# Revit family: CRUi-Red_Amber
name_source: partatom
category: Lighting Fixtures
units: mm (PartAtom-declared; Revit-internal decimal feet)

## family parameters
Always vertical = Yes
Cut with Voids When Loaded = No
Host = Ceiling
Light Source = Yes
OmniClass Number = 23.80.70.11.14.17
OmniClass Title = Direct/Indirect
Part Type = Normal
Room Calculation Point = No
Round Connector Dimension = Use Diameter
Shared = No

## types (14) — shared parameters
Description = LED Cleanroom Recessed Universal
Dimming Lamp Color Temperature Shift = <None>
Emit Shape Visible in Rendering = No
Housing Finish = Metal - Viscor - White
Lamp = LED
Lens Finish = Acrylic - Viscor - Frosted Prismatic P12
Manufacturer = Visioneering By Viscor
Model = CRU
Tilt Angle = 90.00°
URL = https://www.viscor.com
Voltage = 120 V

## per-type parameters (varying)
| type | Apparent Load | Assembly Code | Color Filter | Emit from Rectangle Length | Emit from Rectangle Width | Lamp Wattage | Length | Photometric Web File | Width |
| CRUi-1X4-LED840K35L/35AUNV-DSA | 47 VA |  | 4227327 | 3' - 11 3/4" | 0' - 11 3/4" | 47 VA | 3' - 11 3/4" | CRUi-1X4-LED840K35L_35AUNV-DSA.ies | 0' - 11 3/4" |
| CRUI-2X2-LED840KxxxL/10RUNV-DSA | 30 VA |  | 255 | 1' - 11 3/4" | 1' - 11 3/4" | 30 VA | 1' - 11 3/4" | CRUI-2X2-LED840KxxxL_10RUNV-DSA.ies | 1' - 11 3/4" |
| CRUI-2X4-LED840KxxxL/10RUNV-DSA | 27 VA |  | 255 | 3' - 11 3/4" | 1' - 11 3/4" | 27 VA | 3' - 11 3/4" | CRUI-2X4-LED840KxxxL_10RUNV-DSA.ies | 1' - 11 3/4" |
| CRUi-1X4-LED840K35L/55AUNV-DSA | 74 VA |  | 4227327 | 3' - 11 3/4" | 0' - 11 3/4" | 74 VA | 3' - 11 3/4" | CRUi-1X4-LED840K35L_55AUNV-DSA.ies | 0' - 11 3/4" |
| CRUi-1X4-LED840K35L/70AUNV-DSA | 94 VA |  | 4227327 | 3' - 11 3/4" | 0' - 11 3/4" | 94 VA | 3' - 11 3/4" | CRUi-1X4-LED840K35L_70AUNV-DSA.ies | 0' - 11 3/4" |
| CRUi-1X4-LED840KxxxL/10RUNV-DSA | 31 VA | D5020200 | 255 | 3' - 11 3/4" | 0' - 11 3/4" | 31 VA | 3' - 11 3/4" | CRUi-1X4-LED840KxxxL_10RUNV-DSA.ies | 0' - 11 3/4" |
| CRUi-2X2-LED840KxxxL/35AUNV-DSA | 46 VA |  | 4227327 | 1' - 11 3/4" | 1' - 11 3/4" | 46 VA | 1' - 11 3/4" | CRUi-2X2-LED840KxxxL_35AUNV-DSA.ies | 1' - 11 3/4" |
| CRUi-2X2-LED840KxxxL/55AUNV-DSA | 76 VA |  | 4227327 | 1' - 11 3/4" | 1' - 11 3/4" | 76 VA | 1' - 11 3/4" | CRUi-2X2-LED840KxxxL_55AUNV-DSA.ies | 1' - 11 3/4" |
| CRUi-2X2-LED840KxxxL/70AUNV-DSA | 72 VA |  | 4227327 | 1' - 11 3/4" | 1' - 11 3/4" | 72 VA | 1' - 11 3/4" | CRUi-2X2-LED840KxxxL_70AUNV-DSA.ies | 1' - 11 3/4" |
| CRUi-2X4-LED840KxxxL/20RUNV-DSA | 62 VA |  | 255 | 3' - 11 3/4" | 1' - 11 3/4" | 62 VA | 3' - 11 3/4" | CRUi-2X4-LED840KxxxL_20RUNV-DSA.ies | 1' - 11 3/4" |
| CRUi-2X4-LED840KxxxL/35AUNV-DSA | 41 VA |  | 4227327 | 3' - 11 3/4" | 1' - 11 3/4" | 41 VA | 3' - 11 3/4" | CRUi-2X4-LED840KxxxL_35AUNV-DSA.ies | 1' - 11 3/4" |
| CRUi-2X4-LED840KxxxL/55AUNV-DSA | 61 VA |  | 4227327 | 3' - 11 3/4" | 1' - 11 3/4" | 61 VA | 3' - 11 3/4" | CRUi-2X4-LED840KxxxL_55AUNV-DSA.ies | 1' - 11 3/4" |
| CRUi-2X4-LED840KxxxL/70AUNV-DSA | 81 VA |  | 4227327 | 3' - 11 3/4" | 1' - 11 3/4" | 81 VA | 3' - 11 3/4" | CRUi-2X4-LED840KxxxL_70AUNV-DSA.ies | 1' - 11 3/4" |
| CRUi-2X4-LED840KxxxL/100AUNV-DSA | 122 VA |  | 4227327 | 3' - 11 3/4" | 1' - 11 3/4" | 122 VA | 3' - 11 3/4" | CRUi-2X4-LED840KxxxL_100AUNV-DSA.ies | 1' - 11 3/4" |

## geometry (parser evidence)
native form markers: Sweep x3
no freeform markers — native parametric forms only
